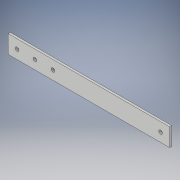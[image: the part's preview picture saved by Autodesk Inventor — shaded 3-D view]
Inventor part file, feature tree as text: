
AUTODESK INVENTOR PART (.ipt)
format: ipt  version: 2018 (Build 220112000, 112)  size: 111,104 bytes
history: native  units: in
note: dims shown in document units (in); Inventor stores cm internally (conversion verified against a paired STEP export)
features: extrude x2, sketch x2
ambient origin geometry x8: Origin, YZ Plane, XZ Plane, XY Plane, X Axis, Y Axis, Z Axis, Center Point
bodies: Solid1 (feature_tree)
feature tree (4):
  extrude  "Extrusion1"  Depth=1.0in
  extrude  "Extrusion2"  Depth=1.0in
  sketch  "Sketch1"  dims[d0=9.0in d1=1.0in]
  sketch  "Sketch2"  dims[d2=0.125in d3=0.0in d4=0.5in d5=0.2031in d6=6.0in d7=0.2031in d8=1.0in d9=0.2031in d10=1.0in d11=0.2031in d12=0.5in d13=0.0in]
